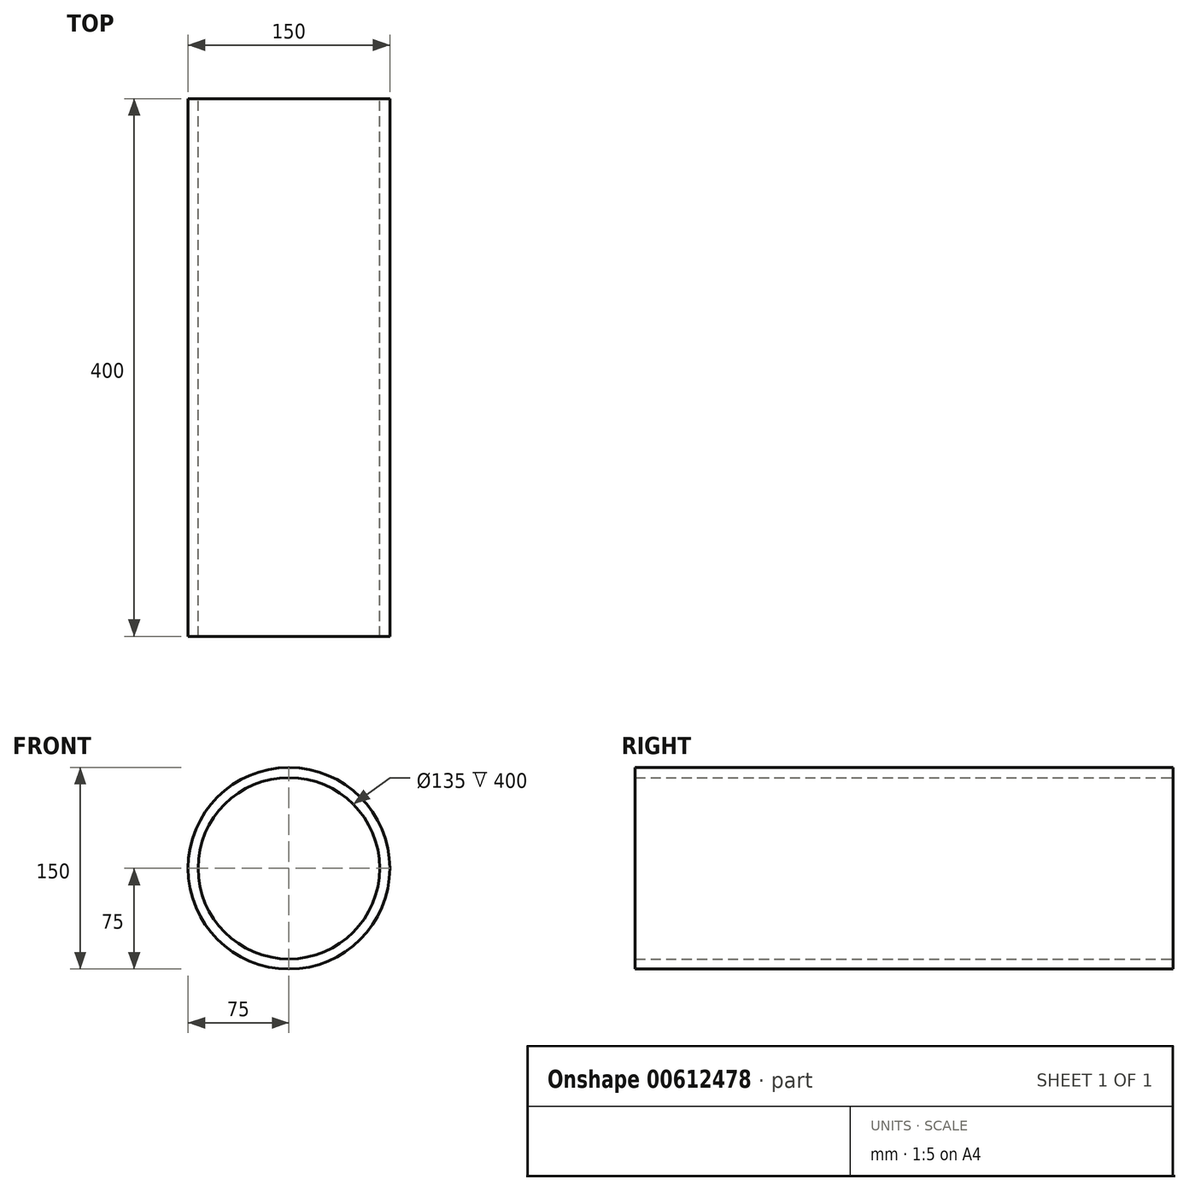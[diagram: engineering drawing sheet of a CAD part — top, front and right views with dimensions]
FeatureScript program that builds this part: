
annotation { "Feature Type Name" : "Feature", "Feature Type Description" : "" }
export const myFeature = defineFeature(function(context is Context, id is Id, definition is map)
    precondition{}
    {
        {
            var Q0;
            Q0=qCreatedBy(makeId("Front.planeOp"),FACE);
            var sketch = newSketch(context, id + "F0", { "sketchPlane" : qUnion([Q0])});
            skCircle(sketch, "E0", {"center": v(0, 0) * mm, "radius": 75 * mm});
            skCircle(sketch, "E1", {"center": v(0, 0) * mm, "radius": 67.5 * mm});
            skSolve(sketch);
        }
        {
            var Q0;
            Q0=makeQuery(id+"F0.imprint","IMPRINT",FACE,{"disambiguationData":[TD([[makeQuery(id+"F0.imprint","IMPRINT",EDGE,{"derivedFrom":sQuery(id+"F0.wireOp",EDGE,"E0")}),1.0]])]});
            var Q1;
            Q1=sQuery(id+"F0.wireOp",EDGE,"E1");
            var Q2;
            Q2=sQuery(id+"F0.wireOp",EDGE,"E0");
            extrude(context, id + "F1", {"entities" : qUnion([Q0]), "surfaceEntities" : qUnion([Q1, Q2]), "depth" : 400 * mm, "offsetDistance" : 25 * mm});
        }
    });
